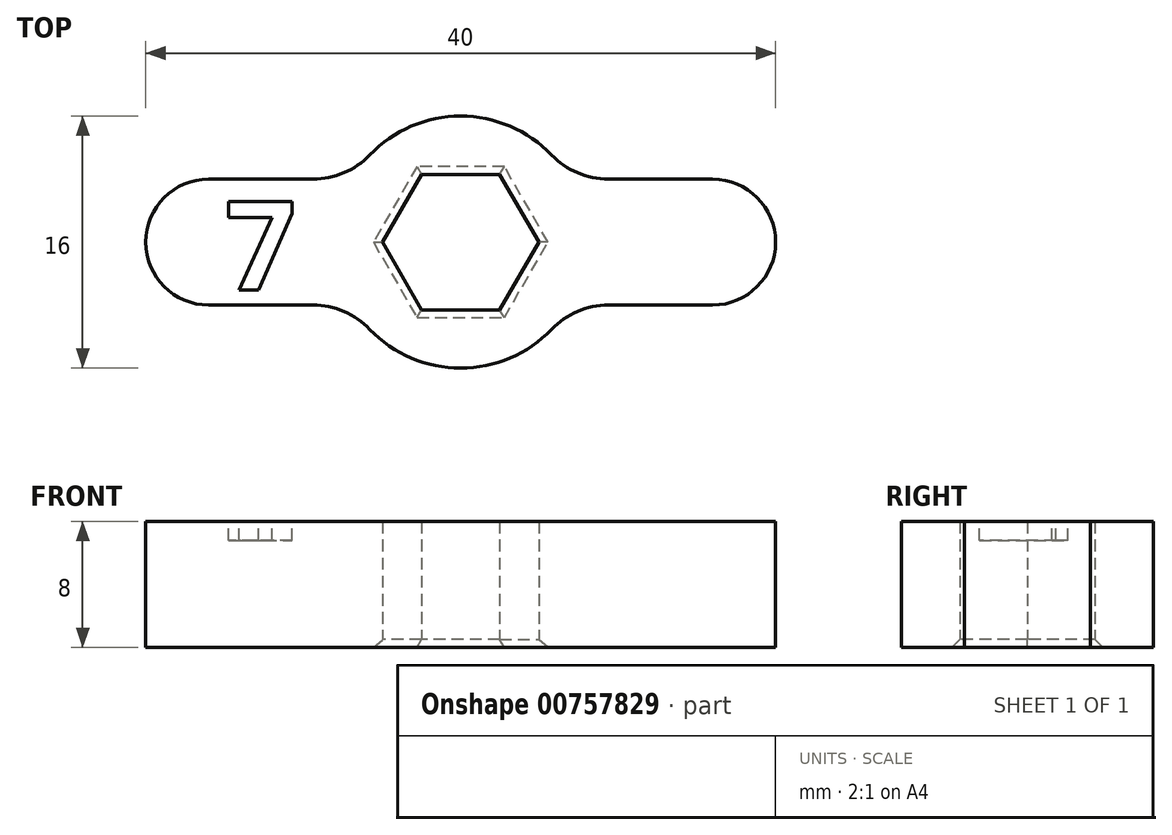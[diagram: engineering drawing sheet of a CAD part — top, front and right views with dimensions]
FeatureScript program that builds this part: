
annotation { "Feature Type Name" : "Feature", "Feature Type Description" : "" }
export const myFeature = defineFeature(function(context is Context, id is Id, definition is map)
    precondition{}
    {
        {
            var Q0;
            Q0=qCreatedBy(makeId("Top.planeOp"),FACE);
            var sketch = newSketch(context, id + "F0", { "sketchPlane" : qUnion([Q0])});
            skCircle(sketch, "E0.cCircle", {"center": v(-4.05, 4.3) * mm, "radius": 4.3 * mm, "construction": true});
            skLineSegment(sketch, "E0.0", {"start": v(0.92, 4.3) * mm, "end": v(-1.57, 0) * mm});
            skLineSegment(sketch, "E0.1", {"start": v(-1.57, 0) * mm, "end": v(-6.53, 0) * mm});
            skLineSegment(sketch, "E0.2", {"start": v(-6.53, 0) * mm, "end": v(-9.01, 4.3) * mm});
            skLineSegment(sketch, "E0.3", {"start": v(-9.01, 4.3) * mm, "end": v(-6.53, 8.6) * mm});
            skLineSegment(sketch, "E0.4", {"start": v(-6.53, 8.6) * mm, "end": v(-1.57, 8.6) * mm});
            skLineSegment(sketch, "E0.5", {"start": v(-1.57, 8.6) * mm, "end": v(0.92, 4.3) * mm});
            skPoint(sketch, "E0.0.midPoint", {"position": v(-0.32, 2.15) * mm});
            skCircle(sketch, "E1", {"center": v(-4.05, 4.3) * mm, "radius": 8 * mm});
            skLineSegment(sketch, "E2.bottom", {"start": v(2.88, 8.3) * mm, "end": v(11.95, 8.3) * mm});
            skLineSegment(sketch, "E2.top", {"start": v(2.88, 0.3) * mm, "end": v(11.95, 0.3) * mm});
            skArc(sketch, "E3", {"start": v(11.95, 8.3) * mm, "mid": v(15.95, 4.3) * mm, "end": v(11.95, 0.3) * mm});
            skLineSegment(sketch, "E4", {"start": v(-4.05, 13.39) * mm, "end": v(-4.05, -5.1) * mm, "construction": true});
            skLineSegment(sketch, "E5.MirrorCS", {"start": v(-10.98, 8.3) * mm, "end": v(-20.05, 8.3) * mm});
            skArc(sketch, "E6.MirrorCS", {"start": v(-20.05, 8.3) * mm, "mid": v(-24.05, 4.3) * mm, "end": v(-20.05, 0.3) * mm});
            skLineSegment(sketch, "E7.MirrorCS", {"start": v(-10.98, 0.3) * mm, "end": v(-20.05, 0.3) * mm});
            skLineSegment(sketch, "E8", {"start": v(-20.05, 4.3) * mm, "end": v(11.95, 4.3) * mm, "construction": true});
            skSolve(sketch);
        }
        {
            var Q0;
            {var subQ0=sQuery(id+"F0.wireOp",EDGE,"E5.MirrorCS");Q0=makeQuery(id+"F0.imprint","IMPRINT",FACE,{"disambiguationData":[TD([[makeQuery(id+"F0.imprint","IMPRINT",EDGE,{"derivedFrom":subQ0}),1.0]])]});}
            var Q1;
            Q1=makeQuery(id+"F0.imprint","IMPRINT",FACE,{"disambiguationData":[TD([[makeQuery(id+"F0.imprint","IMPRINT",EDGE,{"derivedFrom":sQuery(id+"F0.wireOp",EDGE,"E0.0")}),1.0]])]});
            var Q2;
            {var subQ0=sQuery(id+"F0.wireOp",EDGE,"E2.bottom");Q2=makeQuery(id+"F0.imprint","IMPRINT",FACE,{"disambiguationData":[TD([[makeQuery(id+"F0.imprint","IMPRINT",EDGE,{"derivedFrom":subQ0}),-1.0]])]});}
            extrude(context, id + "F1", {"entities" : qUnion([Q0, Q1, Q2]), "depth" : 8 * mm});
        }
        {
            var Q0;
            Q0=makeQuery(id+"F1.opExtrude","CAP_FACE",FACE,{"disambiguationData":[OSD([sQuery(id+"F0.wireOp",EDGE,"E0.0"),sQuery(id+"F0.wireOp",EDGE,"E0.1"),sQuery(id+"F0.wireOp",EDGE,"E0.2"),sQuery(id+"F0.wireOp",EDGE,"E0.3"),sQuery(id+"F0.wireOp",EDGE,"E0.4"),sQuery(id+"F0.wireOp",EDGE,"E0.5"),sQuery(id+"F0.wireOp",EDGE,"E1"),sQuery(id+"F0.wireOp",EDGE,"E2.bottom"),sQuery(id+"F0.wireOp",EDGE,"E2.top"),sQuery(id+"F0.wireOp",EDGE,"E3"),sQuery(id+"F0.wireOp",EDGE,"E5.MirrorCS"),sQuery(id+"F0.wireOp",EDGE,"E6.MirrorCS"),sQuery(id+"F0.wireOp",EDGE,"E7.MirrorCS")])],"isStart":false});
            var sketch = newSketch(context, id + "F2", { "sketchPlane" : qUnion([Q0])});
            skText(sketch, "E9", { "text": "7", "fontName": "OpenSans-Bold.ttf"});
            skLineSegment(sketch, "E10.0", {"start": v(-20.05, 4.3) * mm, "end": v(11.95, 4.3) * mm, "construction": true});
            const initialGuessF2  = {"E9": [-0.019, 0.00126, 1, 0, 0.00566]};
            skSetInitialGuess(sketch, initialGuessF2);
            skSolve(sketch);
        }
        {
            var Q0;
            Q0=qSketchRegion(id+"F2",true);
            extrude(context, id + "F3", {"entities" : qUnion([Q0]), "operationType" : NewBodyOperationType.REMOVE, "oppositeDirection" : true, "depth" : 1.2 * mm});
        }
        {
            var Q0;
            Q0=makeQuery(id+"F1.opExtrude","SWEPT_EDGE",EDGE,{"disambiguationData":[OSD([sQuery(id+"F0.wireOp",EDGE,"E1"),sQuery(id+"F0.wireOp",EDGE,"E2.top")])]});
            var Q1;
            Q1=makeQuery(id+"F1.opExtrude","SWEPT_EDGE",EDGE,{"disambiguationData":[OSD([sQuery(id+"F0.wireOp",EDGE,"E1"),sQuery(id+"F0.wireOp",EDGE,"E7.MirrorCS")])]});
            var Q2;
            Q2=makeQuery(id+"F1.opExtrude","SWEPT_EDGE",EDGE,{"disambiguationData":[OSD([sQuery(id+"F0.wireOp",EDGE,"E1"),sQuery(id+"F0.wireOp",EDGE,"E2.bottom")])]});
            var Q3;
            Q3=makeQuery(id+"F1.opExtrude","SWEPT_EDGE",EDGE,{"disambiguationData":[OSD([sQuery(id+"F0.wireOp",EDGE,"E1"),sQuery(id+"F0.wireOp",EDGE,"E5.MirrorCS")])]});
            fillet(context, id + "F4", {"entities" : qUnion([Q0, Q1, Q2, Q3]), "radius" : 5 * mm, "tangentPropagation" : true, "allowEdgeOverflow" : false});
        }
        {
            var Q0;
            Q0=makeQuery(id+"F1.opExtrude","CAP_EDGE",EDGE,{"disambiguationData":[OSD([sQuery(id+"F0.wireOp",EDGE,"E0.1")])],"isStart":true});
            var Q1;
            Q1=makeQuery(id+"F1.opExtrude","CAP_EDGE",EDGE,{"disambiguationData":[OSD([sQuery(id+"F0.wireOp",EDGE,"E0.2")])],"isStart":true});
            var Q2;
            Q2=makeQuery(id+"F1.opExtrude","CAP_EDGE",EDGE,{"disambiguationData":[OSD([sQuery(id+"F0.wireOp",EDGE,"E0.3")])],"isStart":true});
            var Q3;
            Q3=makeQuery(id+"F1.opExtrude","CAP_EDGE",EDGE,{"disambiguationData":[OSD([sQuery(id+"F0.wireOp",EDGE,"E0.4")])],"isStart":true});
            var Q4;
            Q4=makeQuery(id+"F1.opExtrude","CAP_EDGE",EDGE,{"disambiguationData":[OSD([sQuery(id+"F0.wireOp",EDGE,"E0.5")])],"isStart":true});
            var Q5;
            Q5=makeQuery(id+"F1.opExtrude","CAP_EDGE",EDGE,{"disambiguationData":[OSD([sQuery(id+"F0.wireOp",EDGE,"E0.0")])],"isStart":true});
            chamfer(context, id + "F5", {"entities" : qUnion([Q0, Q1, Q2, Q3, Q4, Q5]), "width" : 0.5 * mm, "tangentPropagation" : true});
        }
    });
